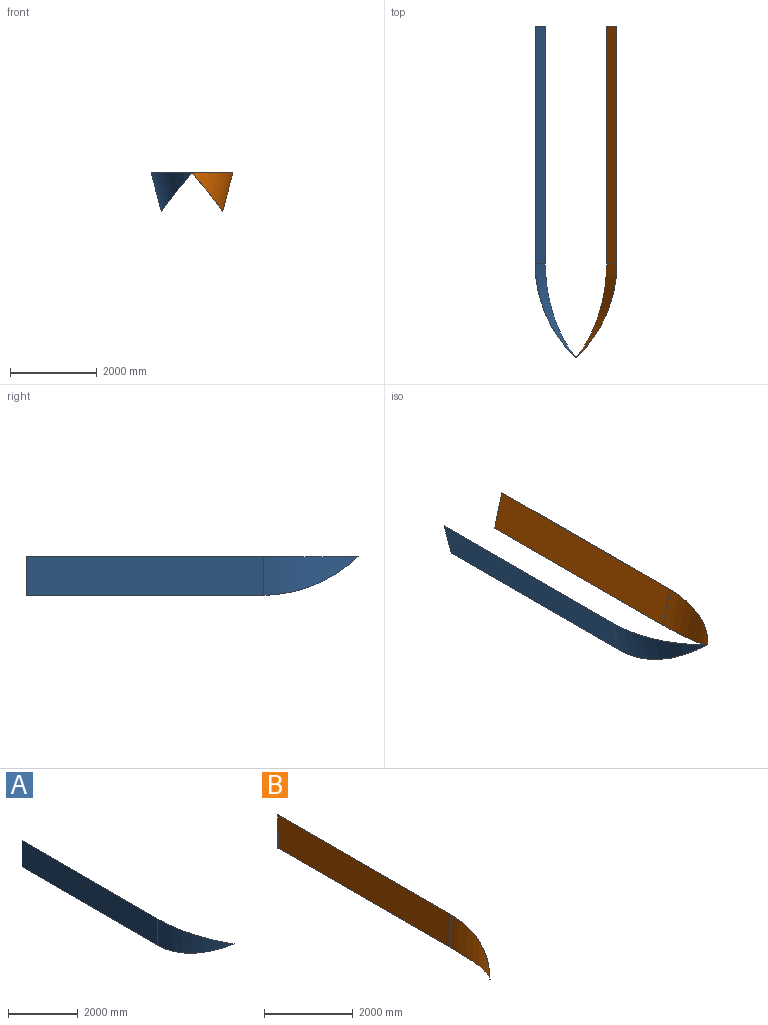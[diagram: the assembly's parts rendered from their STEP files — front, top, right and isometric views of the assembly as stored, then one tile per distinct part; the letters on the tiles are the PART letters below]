
ASSEMBLY  parts=2 mates=1
PART A: 9 faces, bbox 911.9x7658.8x914.4 mm
  f0: cylinder r=3051.18mm len=2172.39mm, axis (0,0,-1), area 1442066.1mm2, adj f3,f5,f7,f8
  f1: cylinder r=3048mm len=2171.12mm, axis (0,0,-1), area 1440056.4mm2, adj f4,f7,f8
  f2: plane 914.4x3.18mm, normal (0,1,0), area 2903.2mm2, adj f3,f4,f5,f6
  f3: plane 5486.4x914.4mm, normal (-1,0,0), area 5016764.2mm2, adj f0,f2,f5,f6
  f4: plane 5486.4x914.4mm, normal (1,0,0), area 5016764.2mm2, adj f1,f2,f5,f6
  f5: plane 5625.56x3.18mm, normal (0,0,1), area 17713.9mm2, adj f0,f2,f3,f4,f8
  f6: plane 5486.4x3.18mm, normal (0,0,-1), area 17419.3mm2, adj f2,f3,f4,f7
  f7: cylinder r=3848.4mm len=2172.39mm, axis (-1,0,0), area 8202.2mm2, adj f0,f1,f6,f8
  f8: plane 2172.39x908.71mm, normal (0.26,0,0.97), area 7639.5mm2, adj f0,f1,f5,f7
PART B: 9 faces, bbox 911.9x7658.8x914.4 mm
  f0: cylinder r=3051.18mm len=2172.39mm, axis (0,0,-1), area 1442087.9mm2, adj f3,f5,f7,f8
  f1: cylinder r=3048mm len=2171.12mm, axis (0,0,-1), area 1440077.4mm2, adj f4,f7,f8
  f2: plane 914.4x3.18mm, normal (0,1,0), area 2903.2mm2, adj f3,f4,f5,f6
  f3: plane 5486.4x914.4mm, normal (1,0,0), area 5016764.2mm2, adj f0,f2,f5,f6
  f4: plane 5486.4x914.4mm, normal (-1,0,0), area 5016764.2mm2, adj f1,f2,f5,f6
  f5: plane 5625.56x3.18mm, normal (0,0,1), area 17713.9mm2, adj f0,f2,f3,f4,f8
  f6: plane 5486.4x3.18mm, normal (0,0,-1), area 17419.3mm2, adj f2,f3,f4,f7
  f7: cylinder r=3848.4mm len=2172.39mm, axis (1,0,0), area 8201.1mm2, adj f0,f1,f6,f8
  f8: plane 2172.39x908.71mm, normal (-0.26,0,0.97), area 7639.5mm2, adj f0,f1,f5,f7
PLACE A rot(axis=(0,-1,0),15deg) t=(78.77,0,332.59)mm fixed
PLACE B rot(axis=(0,1,0),15deg) t=(-868.03,0.06,332.59)mm
MATE planar A.f8 <-> B.f8  axis (0,0,1) through (-1004.25,1248.01,900.28)mm
